# Revit family: KEUCO_14923010000_
name_source: partatom
category: Generic Models
revit_build: Autodesk Revit 2016 (Build: 20150220_1215(x64)
units: mm (PartAtom-declared; Revit-internal decimal feet)

## family parameters
Always vertical = No
Can host rebar = No
Cut with Voids When Loaded = No
Part Type = Normal
Room Calculation Point = No
Round Connector Dimension = Use Diameter
Shared = No
Work Plane-Based = Yes

## types (3) — shared parameters
Default Elevation = 1219 mm
Manufacturer = KEUCO
Serie = Plan
Stange Breite = 340 mm  [stored 1.11549 ft]
URL = https://www.keuco.com
Verwendung = GWC / WP
zero-valued in all types: Gewicht

## per-type parameters (varying)
| type | Ausschreibungstext | Material |
| 14923010000 | KEUCO PLAN Handtuchhalter, einarmig, 14923010000
Hochglanzverchromter Handtuchhalter, einarmig, 
in ästhetischem, funktionalem Design,
aus rundem Rohr, mit flachem Endstopfen, 
ein feststehender runder Haltearm, antistatisch, 
leicht zu reinigen,
Ausladung 340 mm, Durchmesser 22 mm, 
Rosettendurchmesser 55 mm, Rosettendicke 7 mm, 
der Handtuchhalter wird verdeckt angebracht,
Lieferung inkl. korrosionsfreiem Befestigungsmaterial | Verchromt |
| 14923070000 | KEUCO PLAN Handtuchhalter, einarmig, 14923070000
Handtuchhalter aus hochwertigem Edelstahl, einarmig, 
in ästhetischem, funktionalem Design,
aus rundem Rohr, mit flachem Endstopfen, 
ein feststehender runder Haltearm, antistatisch, 
leicht zu reinigen,
Ausladung 340 mm, Durchmesser 22 mm, 
Rosettendurchmesser 55 mm, Rosettendicke 7 mm, 
der Handtuchhalter wird verdeckt angebracht,
Lieferung inkl. korrosionsfreiem Befestigungsmaterial | Edelstahl |
| 14923170000 | KEUCO PLAN Handtuchhalter, einarmig, 14923170000
Handtuchhalter aus silber-eloxiertem Aluminium, einarmig, 
in ästhetischem, funktionalem Design,
aus rundem Rohr, mit flachem Endstopfen, 
ein feststehender runder Haltearm, antistatisch, 
leicht zu reinigen,
Ausladung 340 mm, Durchmesser 22 mm, 
Rosettendurchmesser 55 mm, Rosettendicke 7 mm, 
der Handtuchhalter wird verdeckt angebracht,
Lieferung inkl. korrosionsfreiem Befestigungsmaterial | Edelstahl |

note: column(s) folded — value = type name in every type: Artikelnummer

note: [stored X ft] marks values corroborated as IEEE doubles in the binary element streams (Revit-internal decimal feet)

## geometry (parser evidence)
native form markers: Sweep x2
no freeform markers — native parametric forms only
